# Revit family: 306_c3126af751384ca49c410536e4e37d
name_source: partatom
category: Pipe Accessories
units: mm (PartAtom-declared; Revit-internal decimal feet)

## family parameters
Always vertical = Yes
Cut with Voids When Loaded = No
Part Type = Valve - Breaks Into
Round Connector Dimension = Use Diameter
Shared = No
Work Plane-Based = No

## types (3) — shared parameters
Description = 2-way Motorized ball valve MBA124, PN32 internal/external thread
H1 = 1 mm  [stored 0.00328084 ft]
L2D_Min = 3048 mm
Manufacturer = ESBE
QmdConnectorList = 301;D;302;D
URL = http://www.esbe.eu
X15 = 8 mm  [stored 0.0262467 ft]
X15__ve = -8 mm  [stored -0.0262467 ft]
X16 = 4 mm  [stored 0.0131234 ft]
X16__ve = -4 mm  [stored -0.0131234 ft]
X5 = 3 mm  [stored 0.00984252 ft]
X5__ve = -3 mm
Y0 = 5 mm  [stored 0.0164042 ft]
Y11 = 3 mm  [stored 0.00984252 ft]
Z3 = 11 mm
Z4 = 52 mm
Z5 = 3 mm  [stored 0.00984252 ft]
Z6 = 35 mm
Z6__ve = -35 mm
Z7 = 3 mm  [stored 0.00984252 ft]
magiPartTypeId = 306
magiProductFamilyId = c3126af751384ca49c410536e4e37d

## per-type parameters (varying)
- MBA124 G1  MF 230VAC 2-P 10NM: C=73 mm; CenSd_Y13_6=14 mm  [stored 0.0459318 ft]; D=25 mm; E=29 mm  [stored 0.0951444 ft]; L2D=107 mm; W2D=25 mm  [stored 0.082021 ft]; X1=58 mm; X12=32 mm  [stored 0.104987 ft]; X12__ve=-32 mm; X14=6 mm  [stored 0.019685 ft]; X17=50 mm; X6=14 mm  [stored 0.0459318 ft]; X7=25 mm  [stored 0.082021 ft]; X7__ve=-25 mm; Y1=13 mm  [stored 0.0426509 ft]; Y10=19 mm; Y10__ve=-19 mm; Y12=15 mm  [stored 0.0492126 ft]; Y13=16 mm  [stored 0.0524934 ft]; Y14=14 mm  [stored 0.0459318 ft]; Y2=13 mm  [stored 0.0426509 ft]; Y3=14 mm  [stored 0.0459318 ft]; Y4=15 mm  [stored 0.0492126 ft]; Y5=16 mm  [stored 0.0524934 ft]; Z2=26 mm  [stored 0.0853018 ft]; Z2__ve=-26 mm; magiProductCode=MBA124 G1" MF 230VAC 2-P 10NM; magiProductId=85a19648036d4f89af35f844a8cee4
- MBA124 G3/4  MF 230VAC 2-P 10NM: C=65 mm; CenSd_Y13_6=11 mm; D=20 mm; E=25 mm  [stored 0.082021 ft]; L2D=91 mm; W2D=20 mm  [stored 0.0656168 ft]; X1=50 mm; X12=23 mm; X12__ve=-23 mm; X14=5 mm  [stored 0.0164042 ft]; X17=43 mm; X6=12 mm  [stored 0.0393701 ft]; X7=21 mm; X7__ve=-21 mm; Y1=10 mm  [stored 0.0328084 ft]; Y10=15 mm  [stored 0.0492126 ft]; Y10__ve=-15 mm; Y12=12 mm  [stored 0.0393701 ft]; Y13=13 mm  [stored 0.0426509 ft]; Y14=11 mm; Y2=10 mm  [stored 0.0328084 ft]; Y3=11 mm; Y4=12 mm  [stored 0.0393701 ft]; Y5=12 mm  [stored 0.0393701 ft]; Z2=23 mm; Z2__ve=-23 mm; magiProductCode=MBA124 G3/4" MF 230VAC 2-P 10NM; magiProductId=1bbd9da7e97d43a388a1e79a3666bd
- MBA124 G11/4  MF 230VAC 2-P 10NM: C=75 mm; CenSd_Y13_6=18 mm; D=32 mm; E=34 mm; L2D=111 mm; W2D=32 mm  [stored 0.104987 ft]; X1=60 mm; X12=34 mm; X12__ve=-34 mm  [stored -0.111549 ft]; X14=7 mm  [stored 0.0229659 ft]; X17=52 mm; X6=14 mm  [stored 0.0459318 ft]; X7=26 mm  [stored 0.0853018 ft]; X7__ve=-26 mm; Y1=16 mm  [stored 0.0524934 ft]; Y10=24 mm; Y10__ve=-24 mm; Y12=19 mm; Y13=20 mm  [stored 0.0656168 ft]; Y14=18 mm; Y2=17 mm; Y3=18 mm; Y4=19 mm; Y5=20 mm  [stored 0.0656168 ft]; Z2=31 mm  [stored 0.101706 ft]; Z2__ve=-31 mm  [stored -0.101706 ft]; magiProductCode=MBA124 G11/4" MF 230VAC 2-P 10NM; magiProductId=c8e6d85843534168a0e831422d2876

note: [stored X ft] marks values corroborated as IEEE doubles in the binary element streams (Revit-internal decimal feet)

## geometry (parser evidence)
native form markers: Sweep x3
no freeform markers — native parametric forms only
